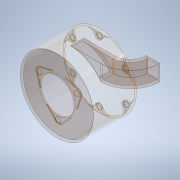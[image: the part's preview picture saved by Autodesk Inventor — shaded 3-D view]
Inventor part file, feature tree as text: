
AUTODESK INVENTOR PART (.ipt)
format: ipt  version: 2020 (Build 240168000, 168)  size: 386,560 bytes
history: native  units: in
note: dims shown in document units (in); Inventor stores cm internally (conversion verified against a paired STEP export)
features: sketch x10, extrude x8, projected_geometry x5, plane x2, shell x1, sweep x1
ambient origin geometry x8: Origin, YZ Plane, XZ Plane, XY Plane, X Axis, Y Axis, Z Axis, Center Point
bodies: Solid1 (feature_tree)
feature tree (27):
  extrude  "Extrusion1"  Depth=3.1496in TaperAngle=0.0deg
  shell  "Shell1"  Thickness=0.1181in
  extrude  "Extrusion2"  Depth=3.1496in TaperAngle=0.0deg
  extrude  "Extrusion3"  Depth=1.5748in
  plane  "Work Plane1"
  extrude  "Extrusion4"  TaperAngle=120.0deg  [1 undecoded]
  extrude  "Extrusion5"  Depth=0.378in
  plane  "Work Plane4"
  sweep  "Sweep2"
  extrude  "Extrusion6"  [1 undecoded]
  extrude  "Extrusion7"  Depth=0.9843in TaperAngle=0.0deg
  extrude  "Extrusion8"  Depth=0.1181in TaperAngle=0.0deg
  sketch  "Sketch1"  dims[d1=5.3543in d2=3.1496in d3=0.0in d4=0.1181in]
  sketch  "Sketch2"  dims[d5=2.5197in d6=3.1496in d7=0.0in]
  sketch  "Sketch3"  dims[d8=0.378in d9=1.5748in]
  projected_geometry  "Projected Loop1"
  sketch  "Sketch4"  dims[d10=120.0deg d11=120.0deg]
  sketch  "Sketch6"  dims[d12=0.378in d13=0.378in]
  projected_geometry  "Projected Loop3"
  sketch  "Sketch9"  dims[d14=1.5748in d15=1.5748in]
  projected_geometry  "Projected Loop4"
  sketch  "Sketch10"  dims[d16=0.06in d17=0.0in d18=-0.9843in]
  sketch  "Sketch11"  dims[d24=1.1811in d25=0.9843in d26=0.0in]
  projected_geometry  "Projected Loop5"
  sketch  "Sketch12"  dims[d27=0.1181in d28=2.2201in d29=0.0in]
  projected_geometry  "Projected Loop6"
  sketch  "Sketch13"  dims[d37=0.0in d38=0.0in d39=0.0591in d40=0.0591in d41=0.0591in d42=0.0591in d43=0.0591in d44=0.0591in d45=0.0591in d46=0.9843in d47=0.9843in d48=0.9843in d49=0.9843in d50=0.9843in d51=0.9843in d52=0.0591in d53=0.0in d54=120.0deg d55=120.0deg d56=120.0deg d57=120.0deg d58=0.378in d59=0.378in d60=0.378in d61=0.378in d62=0.378in d63=0.378in d64=2.2638in d65=2.2638in d66=2.2638in d67=2.2638in d68=2.2638in d69=2.2638in d70=0.0591in d71=0.0591in d72=0.0591in d73=0.0591in d74=0.0591in d75=0.0591in d76=0.7874in d77=0.7874in d78=0.7874in d79=0.7874in d80=0.7874in d81=0.7874in d82=0.7874in d83=0.7874in d84=0.7874in d85=0.7874in d86=0.7874in d87=0.7874in d88=0.1181in d89=0.0in d90=0.378in d91=2.2638in d92=2.3622in d94=360.0deg d96=0.06in d97=0.0in]
note: 2 required parameter values undecoded (feature->parameter linkage not recoverable at this tier; creation-order binding heuristic only, values carry confidence <= 0.55)
